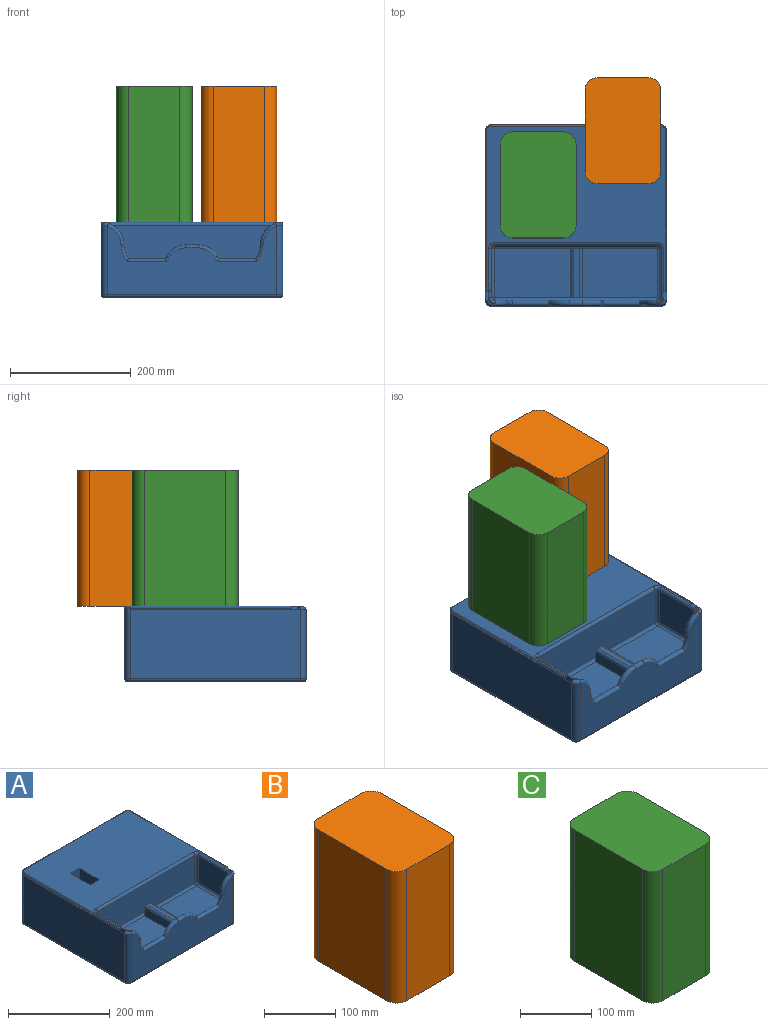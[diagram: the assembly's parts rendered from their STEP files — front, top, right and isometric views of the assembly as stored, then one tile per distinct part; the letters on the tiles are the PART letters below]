
ASSEMBLY  parts=3 mates=2
PART A: 81 faces, bbox 301.6x301.6x126.1 mm
  f0: plane 296x273mm, normal (0,0,1), area 56244.4mm2, adj f14,f15,f29,f34,f39,f43,f46,f50
  f1: plane 126x80mm, normal (0,0,1), area 10080mm2, adj f31,f36,f37,f72
  f2: plane 280x113.42mm, normal (0,-1,0), area 19310.8mm2, adj f16,f17,f18,f19,f20,f23,f28,f33
  f3: plane 80x65mm, normal (1,0,0), area 5194.2mm2, adj f36,f40,f44,f46,f48,f49
  f4: plane 270x61.33mm, normal (0,1,0), area 4686.3mm2, adj f16,f17,f18,f19,f20,f23,f27,f28
  f5: plane 80x65mm, normal (-1,0,0), area 5194.2mm2, adj f21,f24,f26,f27,f29,f30
  f6: plane 280x114.61mm, normal (1,0,0), area 32091.7mm2, adj f21,f55,f58,f63
  f7: plane 280x118mm, normal (0,1,0), area 33040mm2, adj f52,f53,f55,f66
  f8: plane 280x114.61mm, normal (-1,0,0), area 32091.7mm2, adj f49,f53,f57,f62
  f9: plane 290x290mm, normal (0,0,-1), area 84078.5mm2, adj f59,f60,f61,f62,f63,f64,f65,f66
  f10: plane 270x65mm, normal (0,-1,0), area 17550mm2, adj f30,f31,f39,f40
  f11: plane 125x80mm, normal (0,0,1), area 10000mm2, adj f26,f31,f37,f70
  f12: cylinder r=37.5mm len=11.54mm, axis (0,-1,0), area 19.1mm2, adj f45,f47,f49,f67
  f13: cylinder r=37.5mm len=11.54mm, axis (0,-1,0), area 19.1mm2, adj f19,f21,f22,f68
  f14: plane 5x3.28mm, normal (0,-1,0), area 5.9mm2, adj f0,f48,f49,f50
  f15: plane 5x3.28mm, normal (0,-1,0), area 5.9mm2, adj f0,f21,f24,f51
  f16: cylinder r=5mm len=64.81mm, axis (1,0,0), area 980.2mm2, adj f2,f4,f17,f18
  f17: torus R=42.5mm, axis (0,-1,0), area 416.4mm2, adj f2,f4,f16,f19
  f18: torus R=42.5mm, axis (0,-1,0), area 93.1mm2, adj f2,f4,f16,f20
  f19: torus R=32.5mm, axis (0,-1,0), area 658.3mm2, adj f2,f4,f13,f17,f22,f68
  f20: torus R=32.5mm, axis (0,-1,0), area 587mm2, adj f2,f4,f18,f23
  f21: cylinder r=5mm len=284.97mm, axis (0,-1,0), area 794.1mm2, adj f5,f6,f13,f15,f22,f24,f51,f55
  f22: bspline ~12.65x12.22mm, area 88.8mm2, adj f13,f19,f21,f27
  f23: cylinder r=5mm len=20.1mm, axis (1,0,0), area 315.7mm2, adj f2,f4,f20,f28
  f24: cylinder r=5mm len=5.39mm, axis (0,0,1), area 3mm2, adj f5,f15,f21,f29
  f25: sphere r=5mm, area 39.3mm2, adj f26,f30,f31
  f26: cylinder r=5mm len=80mm, axis (0,1,0), area 628.3mm2, adj f5,f11,f25,f32
  f27: cylinder r=5mm len=64.61mm, axis (0,0,-1), area 500mm2, adj f4,f5,f22,f32
  f28: torus R=32.5mm, axis (0,-1,0), area 587mm2, adj f2,f4,f23,f33
  f29: cylinder r=5mm len=70mm, axis (0,-1,0), area 535.5mm2, adj f0,f5,f24,f34
  f30: cylinder r=5mm len=65mm, axis (0,0,-1), area 510.5mm2, adj f5,f10,f25,f34
  f31: cylinder r=5mm len=270mm, axis (-1,0,0), area 2120.6mm2, adj f1,f10,f11,f25,f35,f71
  f32: sphere r=5mm, area 39.3mm2, adj f26,f27,f37
  f33: torus R=42.5mm, axis (0,-1,0), area 93.1mm2, adj f2,f4,f28,f38
  f34: torus R=10mm, axis (0,0,1), area 84.1mm2, adj f0,f29,f30,f39
  f35: sphere r=5mm, area 39.3mm2, adj f31,f36,f40
  f36: cylinder r=5mm len=80mm, axis (0,-1,0), area 628.3mm2, adj f1,f3,f35,f41
  f37: cylinder r=5mm len=270mm, axis (1,0,0), area 2120.6mm2, adj f1,f4,f11,f32,f41,f69
  f38: cylinder r=5mm len=64.81mm, axis (1,0,0), area 980.2mm2, adj f2,f4,f33,f42
  f39: cylinder r=5mm len=270mm, axis (1,0,0), area 2120.6mm2, adj f0,f10,f34,f43
  f40: cylinder r=5mm len=65mm, axis (0,0,-1), area 510.5mm2, adj f3,f10,f35,f43
  f41: sphere r=5mm, area 39.3mm2, adj f36,f37,f44
  f42: torus R=42.5mm, axis (0,-1,0), area 416.4mm2, adj f2,f4,f38,f45
  f43: torus R=10mm, axis (0,0,1), area 84.1mm2, adj f0,f39,f40,f46
  f44: cylinder r=5mm len=64.61mm, axis (0,0,-1), area 500mm2, adj f3,f4,f41,f47
  f45: torus R=32.5mm, axis (0,-1,0), area 658.3mm2, adj f2,f4,f12,f42,f47,f67
  f46: cylinder r=5mm len=70mm, axis (0,1,0), area 535.5mm2, adj f0,f3,f43,f48
  f47: bspline ~14.48x11.62mm, area 88.8mm2, adj f12,f44,f45,f49
  f48: cylinder r=5mm len=5.39mm, axis (0,0,-1), area 3mm2, adj f3,f14,f46,f49
  f49: cylinder r=5mm len=284.97mm, axis (0,-1,0), area 794.1mm2, adj f3,f8,f12,f14,f47,f48,f50,f53
  f50: cylinder r=2mm len=265mm, axis (0,1,0), area 1201.2mm2, adj f0,f14,f49,f54
  f51: cylinder r=2mm len=265mm, axis (0,-1,0), area 1201.2mm2, adj f0,f15,f21,f56
  f52: cylinder r=2mm len=280mm, axis (1,0,0), area 879.6mm2, adj f0,f7,f54,f56
  f53: cylinder r=10mm len=118mm, axis (0,0,1), area 1844.7mm2, adj f7,f8,f49,f54,f64
  f54: torus R=8mm, axis (0,0,1), area 49.4mm2, adj f0,f49,f50,f52,f53
  f55: cylinder r=10mm len=118mm, axis (0,0,-1), area 1844.7mm2, adj f6,f7,f21,f56,f65
  f56: torus R=8mm, axis (0,0,1), area 49.4mm2, adj f0,f21,f51,f52,f55
  f57: cylinder r=10mm len=114.61mm, axis (0,0,1), area 1791mm2, adj f2,f8,f60,f67
  f58: cylinder r=10mm len=114.61mm, axis (0,0,-1), area 1791mm2, adj f2,f6,f61,f68
  f59: cylinder r=5mm len=280mm, axis (1,0,0), area 2199.1mm2, adj f2,f9,f60,f61
  f60: torus R=5mm, axis (0,0,1), area 101mm2, adj f9,f57,f59,f62
  f61: torus R=5mm, axis (0,0,1), area 101mm2, adj f9,f58,f59,f63
  f62: cylinder r=5mm len=280mm, axis (0,-1,0), area 2199.1mm2, adj f8,f9,f60,f64
  f63: cylinder r=5mm len=280mm, axis (0,1,0), area 2199.1mm2, adj f6,f9,f61,f65
  f64: torus R=5mm, axis (0,0,1), area 101mm2, adj f9,f53,f62,f66
  f65: torus R=5mm, axis (0,0,1), area 101mm2, adj f9,f55,f63,f66
  f66: cylinder r=5mm len=280mm, axis (-1,0,0), area 2199.1mm2, adj f7,f9,f64,f65
  f67: bspline ~13.39x12.1mm, area 114.5mm2, adj f12,f45,f49,f57
  f68: bspline ~13.39x12.1mm, area 114.5mm2, adj f13,f19,f21,f58
  f69: plane 25x19mm, normal (0,-1,0), area 464.3mm2, adj f37,f70,f72,f73,f74,f75
  f70: plane 80x20mm, normal (1,0,0), area 1600mm2, adj f11,f69,f71,f74
  f71: plane 25x19mm, normal (0,1,0), area 464.3mm2, adj f31,f70,f72,f73,f74,f75
  f72: plane 80x20mm, normal (-1,0,0), area 1600mm2, adj f1,f69,f71,f75
  f73: plane 80x9mm, normal (0,0,1), area 720mm2, adj f69,f71,f74,f75
  f74: cylinder r=5mm len=80mm, axis (0,-1,0), area 628.3mm2, adj f69,f70,f71,f73
  f75: cylinder r=5mm len=80mm, axis (0,1,0), area 628.3mm2, adj f69,f71,f72,f73
  f76: plane 25x25mm, normal (0,-1,0), area 625mm2, adj f0,f77,f79,f80
  f77: plane 55.16x52.58mm, normal (1,0,0), area 2574.1mm2, adj f0,f76,f78,f80
  f78: plane 25x25mm, normal (0,1,0), area 625mm2, adj f0,f77,f79,f80
  f79: plane 55.16x52.58mm, normal (-1,0,0), area 2574.1mm2, adj f0,f76,f78,f80
  f80: cylinder r=27.58mm len=55.16mm, axis (1,0,0), area 2166.3mm2, adj f76,f77,f78,f79
PART B: 10 faces, bbox 125x175.2x225 mm
  f0: plane 225x85mm, normal (0,-1,0), area 19125mm2, adj f1,f7,f8,f9
  f1: cylinder r=20mm len=225mm, axis (0,0,-1), area 7068.6mm2, adj f0,f2,f8,f9
  f2: plane 225x135.16mm, normal (1,0,0), area 30411.8mm2, adj f1,f3,f8,f9
  f3: cylinder r=20mm len=225mm, axis (0,0,-1), area 7068.6mm2, adj f2,f4,f8,f9
  f4: plane 225x85mm, normal (0,1,0), area 19125mm2, adj f3,f5,f8,f9
  f5: cylinder r=20mm len=225mm, axis (0,0,-1), area 7068.6mm2, adj f4,f6,f8,f9
  f6: plane 225x135.16mm, normal (-1,0,0), area 30411.8mm2, adj f5,f7,f8,f9
  f7: cylinder r=20mm len=225mm, axis (0,0,-1), area 7068.6mm2, adj f0,f6,f8,f9
  f8: plane 175.16x125mm, normal (0,0,1), area 21552.1mm2, adj f0,f1,f2,f3,f4,f5,f6,f7
  f9: plane 175.16x125mm, normal (0,0,-1), area 21552.1mm2, adj f0,f1,f2,f3,f4,f5,f6,f7
PART C: 10 faces, bbox 125x175.2x225 mm
  f0: plane 225x85mm, normal (0,-1,0), area 19125mm2, adj f1,f7,f8,f9
  f1: cylinder r=20mm len=225mm, axis (0,0,-1), area 7068.6mm2, adj f0,f2,f8,f9
  f2: plane 225x135.16mm, normal (1,0,0), area 30411.8mm2, adj f1,f3,f8,f9
  f3: cylinder r=20mm len=225mm, axis (0,0,-1), area 7068.6mm2, adj f2,f4,f8,f9
  f4: plane 225x85mm, normal (0,1,0), area 19125mm2, adj f3,f5,f8,f9
  f5: cylinder r=20mm len=225mm, axis (0,0,-1), area 7068.6mm2, adj f4,f6,f8,f9
  f6: plane 225x135.16mm, normal (-1,0,0), area 30411.8mm2, adj f5,f7,f8,f9
  f7: cylinder r=20mm len=225mm, axis (0,0,-1), area 7068.6mm2, adj f0,f6,f8,f9
  f8: plane 175.16x125mm, normal (0,0,1), area 21552.1mm2, adj f0,f1,f2,f3,f4,f5,f6,f7
  f9: plane 175.16x125mm, normal (0,0,-1), area 21552.1mm2, adj f0,f1,f2,f3,f4,f5,f6,f7
PLACE A at identity fixed
PLACE B t=(1,108.19,125)mm
PLACE C t=(-206.82,18.44,125)mm
MATE planar A.f55 <-> B.f9  axis (0,0,1) through (-10,116.16,125)mm
MATE planar A.f0 <-> C.f9  axis (0,0,1) through (-148.22,26.47,125)mm
